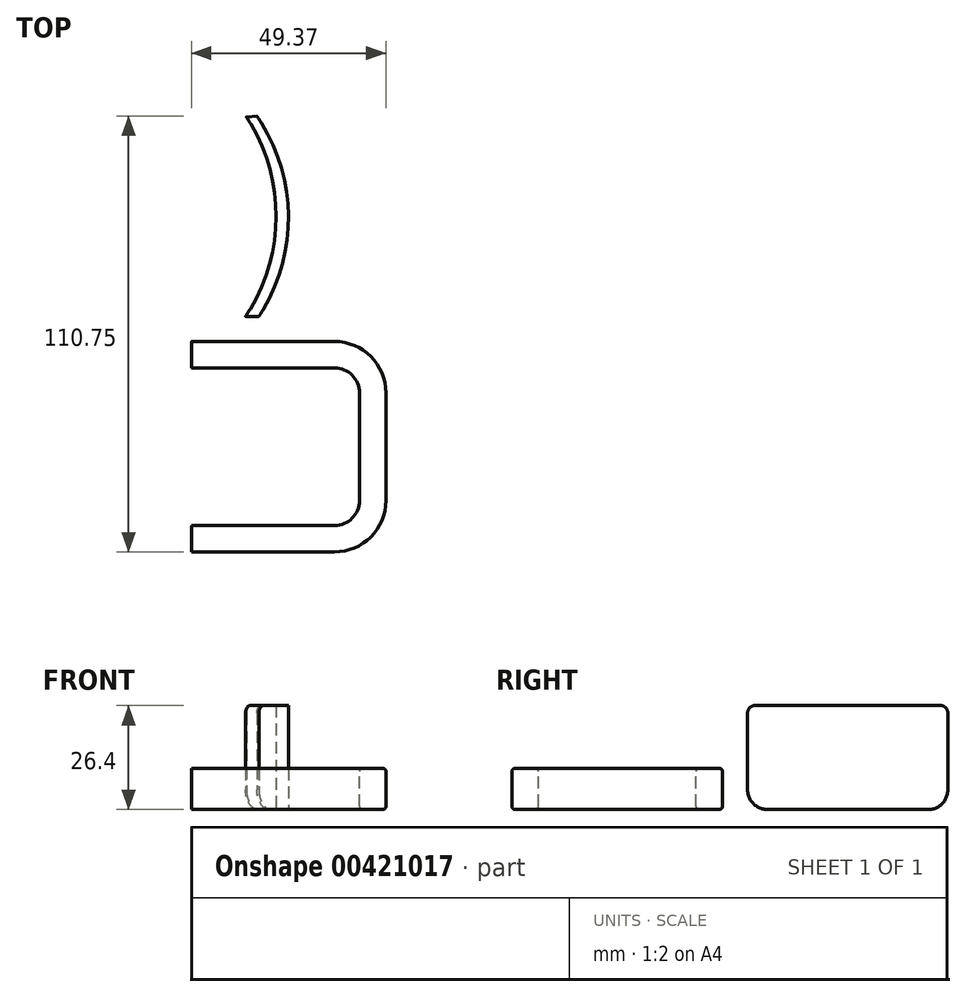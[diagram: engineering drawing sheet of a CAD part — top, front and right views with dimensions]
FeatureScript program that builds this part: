
annotation { "Feature Type Name" : "Feature", "Feature Type Description" : "" }
export const myFeature = defineFeature(function(context is Context, id is Id, definition is map)
    precondition{}
    {
        {
            var Q0;
            Q0=qCreatedBy(makeId("Top.planeOp"),FACE);
            var sketch = newSketch(context, id + "F0", { "sketchPlane" : qUnion([Q0])});
            skLineSegment(sketch, "E0", {"start": v(0, 0) * mm, "end": v(36.3, 0) * mm});
            skLineSegment(sketch, "E1", {"start": v(42.65, -6.35) * mm, "end": v(42.65, -33.7) * mm});
            skLineSegment(sketch, "E2", {"start": v(36.3, -40.05) * mm, "end": v(0, -40.05) * mm});
            skPoint(sketch, "E3.visualSharp", {"position": v(42.65, 0) * mm});
            skArc(sketch, "E3.filletArc", {"start": v(42.65, -6.35) * mm, "mid": v(40.79, -1.86) * mm, "end": v(36.3, 0) * mm});
            skPoint(sketch, "E4.visualSharp", {"position": v(42.65, -40.05) * mm});
            skArc(sketch, "E4.filletArc", {"start": v(36.3, -40.05) * mm, "mid": v(40.79, -38.19) * mm, "end": v(42.65, -33.7) * mm});
            skSolve(sketch);
        }
        {
            var Q0;
            Q0=qCreatedBy(makeId("Right.planeOp"),FACE);
            var sketch = newSketch(context, id + "F1", { "sketchPlane" : qUnion([Q0])});
            skLineSegment(sketch, "E5.bottom", {"start": v(0.76, 0) * mm, "end": v(5.96, 0) * mm});
            skLineSegment(sketch, "E5.top", {"start": v(0.76, 10.41) * mm, "end": v(5.96, 10.41) * mm});
            skLineSegment(sketch, "E5.left", {"start": v(0, 0.76) * mm, "end": v(0, 9.65) * mm});
            skLineSegment(sketch, "E5.right", {"start": v(6.72, 0.76) * mm, "end": v(6.72, 9.65) * mm});
            skPoint(sketch, "E6.visualSharp", {"position": v(6.72, 10.41) * mm});
            skArc(sketch, "E6.filletArc", {"start": v(6.72, 9.65) * mm, "mid": v(6.5, 10.19) * mm, "end": v(5.96, 10.41) * mm});
            skPoint(sketch, "E7.visualSharp", {"position": v(0, 10.41) * mm});
            skArc(sketch, "E7.filletArc", {"start": v(0.76, 10.41) * mm, "mid": v(0.22, 10.19) * mm, "end": v(0, 9.65) * mm});
            skPoint(sketch, "E8.visualSharp", {"position": v(0, 0) * mm});
            skArc(sketch, "E8.filletArc", {"start": v(0, 0.76) * mm, "mid": v(0.22, 0.22) * mm, "end": v(0.76, 0) * mm});
            skPoint(sketch, "E9.visualSharp", {"position": v(6.72, 0) * mm});
            skArc(sketch, "E9.filletArc", {"start": v(5.96, 0) * mm, "mid": v(6.5, 0.22) * mm, "end": v(6.72, 0.76) * mm});
            skSolve(sketch);
        }
        {
            var Q0;
            Q0=makeQuery(id+"F1.imprint","IMPRINT",FACE,{"disambiguationData":[TD([[makeQuery(id+"F1.imprint","IMPRINT",EDGE,{"derivedFrom":sQuery(id+"F1.wireOp",EDGE,"E5.bottom")}),1.0]])]});
            var Q1;
            Q1=sQuery(id+"F0.wireOp",EDGE,"E0");
            var Q2;
            Q2=sQuery(id+"F0.wireOp",EDGE,"E3.filletArc");
            var Q3;
            Q3=sQuery(id+"F0.wireOp",EDGE,"E1");
            var Q4;
            Q4=sQuery(id+"F0.wireOp",EDGE,"E4.filletArc");
            var Q5;
            Q5=sQuery(id+"F0.wireOp",EDGE,"E2");
            sweep(context, id + "F2", {"profiles" : qUnion([Q0]), "path" : qUnion([Q1, Q2, Q3, Q4, Q5])});
        }
        {
            var Q0;
            Q0=qCreatedBy(makeId("Top.planeOp"),FACE);
            var sketch = newSketch(context, id + "F3", { "sketchPlane" : qUnion([Q0])});
            skArc(sketch, "E10", {"start": v(17.09, 13.09) * mm, "mid": v(24.6, 38.6) * mm, "end": v(16.6, 63.98) * mm});
            skArc(sketch, "E11", {"start": v(13.7, 13.09) * mm, "mid": v(21.45, 38.38) * mm, "end": v(13.94, 63.74) * mm});
            skLineSegment(sketch, "E12", {"start": v(17.09, 13.09) * mm, "end": v(13.7, 13.09) * mm});
            skLineSegment(sketch, "E13", {"start": v(16.6, 63.98) * mm, "end": v(13.94, 63.74) * mm});
            skSolve(sketch);
        }
        {
            var Q0;
            Q0=makeQuery(id+"F3.imprint","IMPRINT",FACE,{"disambiguationData":[TD([[makeQuery(id+"F3.imprint","IMPRINT",EDGE,{"derivedFrom":sQuery(id+"F3.wireOp",EDGE,"E10")}),1.0]])]});
            extrude(context, id + "F4", {"entities" : qUnion([Q0]), "depth" : 26.4 * mm});
        }
        {
            var Q0;
            Q0=makeQuery(id+"F4.opExtrude","CAP_EDGE",EDGE,{"disambiguationData":[OSD([sQuery(id+"F3.wireOp",EDGE,"E13")])],"isStart":true});
            var Q1;
            Q1=makeQuery(id+"F4.opExtrude","CAP_EDGE",EDGE,{"disambiguationData":[OSD([sQuery(id+"F3.wireOp",EDGE,"E12")])],"isStart":true});
            fillet(context, id + "F5", {"entities" : qUnion([Q0, Q1]), "radius" : 5 * mm, "tangentPropagation" : true, "allowEdgeOverflow" : false});
        }
        {
            var Q0;
            Q0=makeQuery(id+"F4.opExtrude","CAP_EDGE",EDGE,{"disambiguationData":[OSD([sQuery(id+"F3.wireOp",EDGE,"E13")])],"isStart":false});
            var Q1;
            Q1=makeQuery(id+"F4.opExtrude","CAP_EDGE",EDGE,{"disambiguationData":[OSD([sQuery(id+"F3.wireOp",EDGE,"E12")])],"isStart":false});
            fillet(context, id + "F6", {"entities" : qUnion([Q0, Q1]), "radius" : 1.93 * mm, "tangentPropagation" : true, "allowEdgeOverflow" : false});
        }
    });
